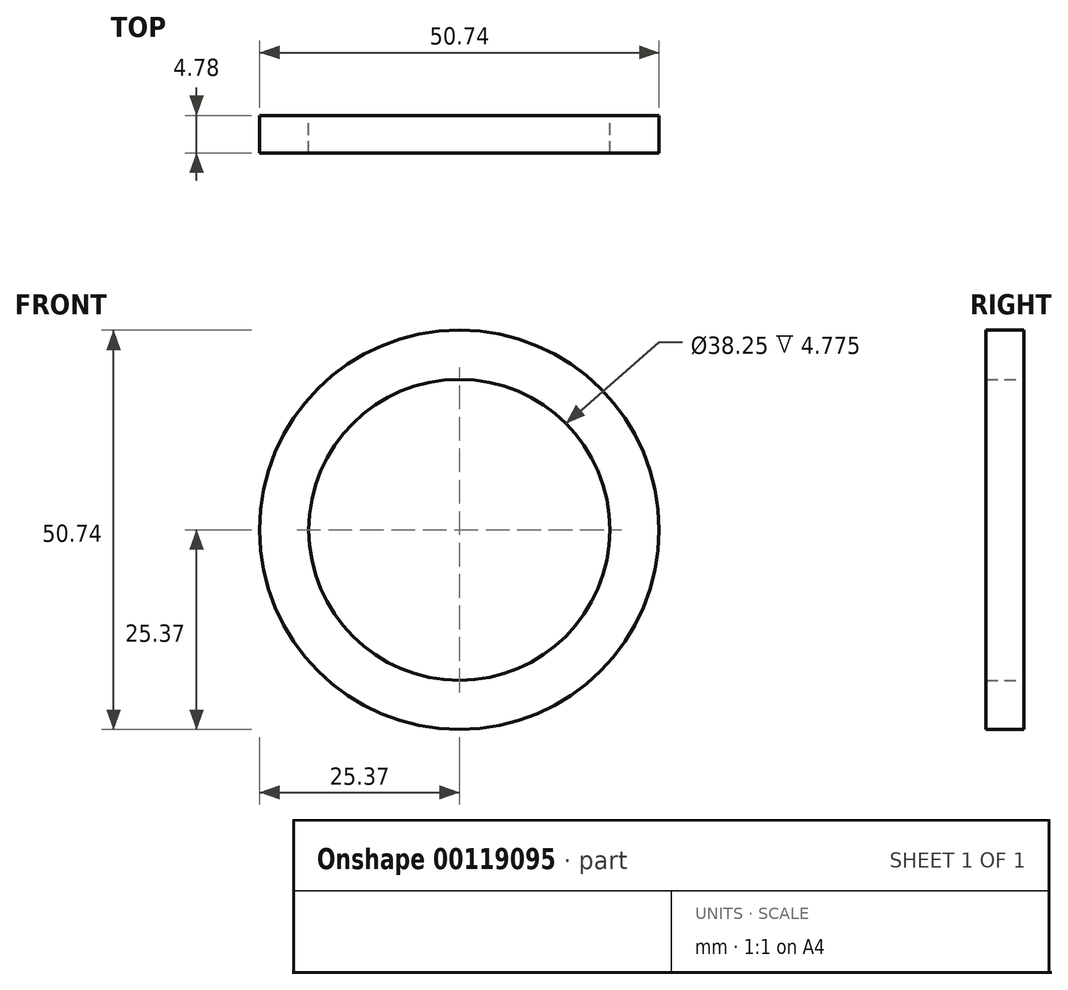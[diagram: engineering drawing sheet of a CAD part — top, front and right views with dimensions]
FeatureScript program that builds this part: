
annotation { "Feature Type Name" : "Feature", "Feature Type Description" : "" }
export const myFeature = defineFeature(function(context is Context, id is Id, definition is map)
    precondition{}
    {
        {
            var Q0;
            Q0=qCreatedBy(makeId("Front.planeOp"),FACE);
            var sketch = newSketch(context, id + "F0", { "sketchPlane" : qUnion([Q0])});
            skCircle(sketch, "E0", {"center": v(0, 0) * mm, "radius": 25.37 * mm});
            skCircle(sketch, "E1", {"center": v(0, 0) * mm, "radius": 19.13 * mm});
            skSolve(sketch);
        }
        {
            var Q0;
            Q0=makeQuery(id+"F0.imprint","IMPRINT",FACE,{"disambiguationData":[TD([[makeQuery(id+"F0.imprint","IMPRINT",EDGE,{"derivedFrom":sQuery(id+"F0.wireOp",EDGE,"E0")}),1.0]])]});
            extrude(context, id + "F1", {"entities" : qUnion([Q0]), "depth" : 4.78 * mm});
        }
    });
